# Revit family: IS_TonicII_A6340_BIM_GB
name_source: partatom
category: Plumbing Fixtures
revit_build: Autodesk Revit MEP 2012 (Build: 20110309_2315(x64)
units: mm (PartAtom-declared; Revit-internal decimal feet)

## types (1)
- A6340AA-TONIC II SL Bath shower mixer built-in kit 2 (requires Easy-box A1000NU)
    AreaUnits = millimeters
    Assembly Code = C1030200
    AssetType = Fixed
    BIMObjectName = ISI_IdealStandard_ShowerMixers_TonicII_A6340
    BarCode = 4015413335089
    Brand = Ideal Standard
    ConnectionType = Plumbing
    Default Elevation = 1219 mm
    Description = Tonic ii single lever built-in shower mixer with diverter
    DurationUnit = year
    ECA = No
    ExpectedLife = 30
    FaucetFunction = MIXED
    FaucetOperation = Other
    FaucetTopDescription = Lever
    FaucetType = Other
    Features = Single lever built-in shower mixer with diverter
    Finish = Chrome
    IfcExportAs = IfcValveType
    IfcExportType = FAUCET
    InstallationDate = 1900-12-31T23:59:59
    InstallationInstructions = www.idealspec.co.uk/resources.html
    LinearUnits = millimeters
    ManufacturerURL = www.idealspec.co.uk
    Model = A6340AA
    ModelNumber = A6340AA
    ModelReference = Tonic ii single lever built-in shower mixer with diverter
    NBSDescription = Shower mixers
    NBSReference = 45-35-70/335
    Name = ShowerMixers_TonicII_A6340_IdealStandard
    NettWeight = 1.2 Kg
    NominalDepth = 163 mm
    NominalHeight = 60 mm
    NominalLength = 163 mm
    NominalWidth = 163 mm
    ProductInformation = www.idealspec.co.uk/assets/datasheet/A6340AA
    Shape = Sculptured
    Size = 61 x 163 x 163 mm
    Space = Internal
    SpareParts = www.fastpart-spares.co.uk
    SustainabilityPerformance = Can be recycled
    TestPressure = 10 Bar
    URL = www.idealspec.co.uk
    Uniclass2 = Pr_40_20_87_78
    Version = 1
    VolumeUnits = Litres
    WRAS = No
    WarrantyDescription = Manufacturers warranty
    WarrantyDurationParts = 5
    WarrantyDurationUnit = year
    WarrantyStartDate = 1900-12-31T23:59:59
    WaterEfficientProduct = No

## geometry (parser evidence)
native form markers: Sweep x3
no freeform markers — native parametric forms only
